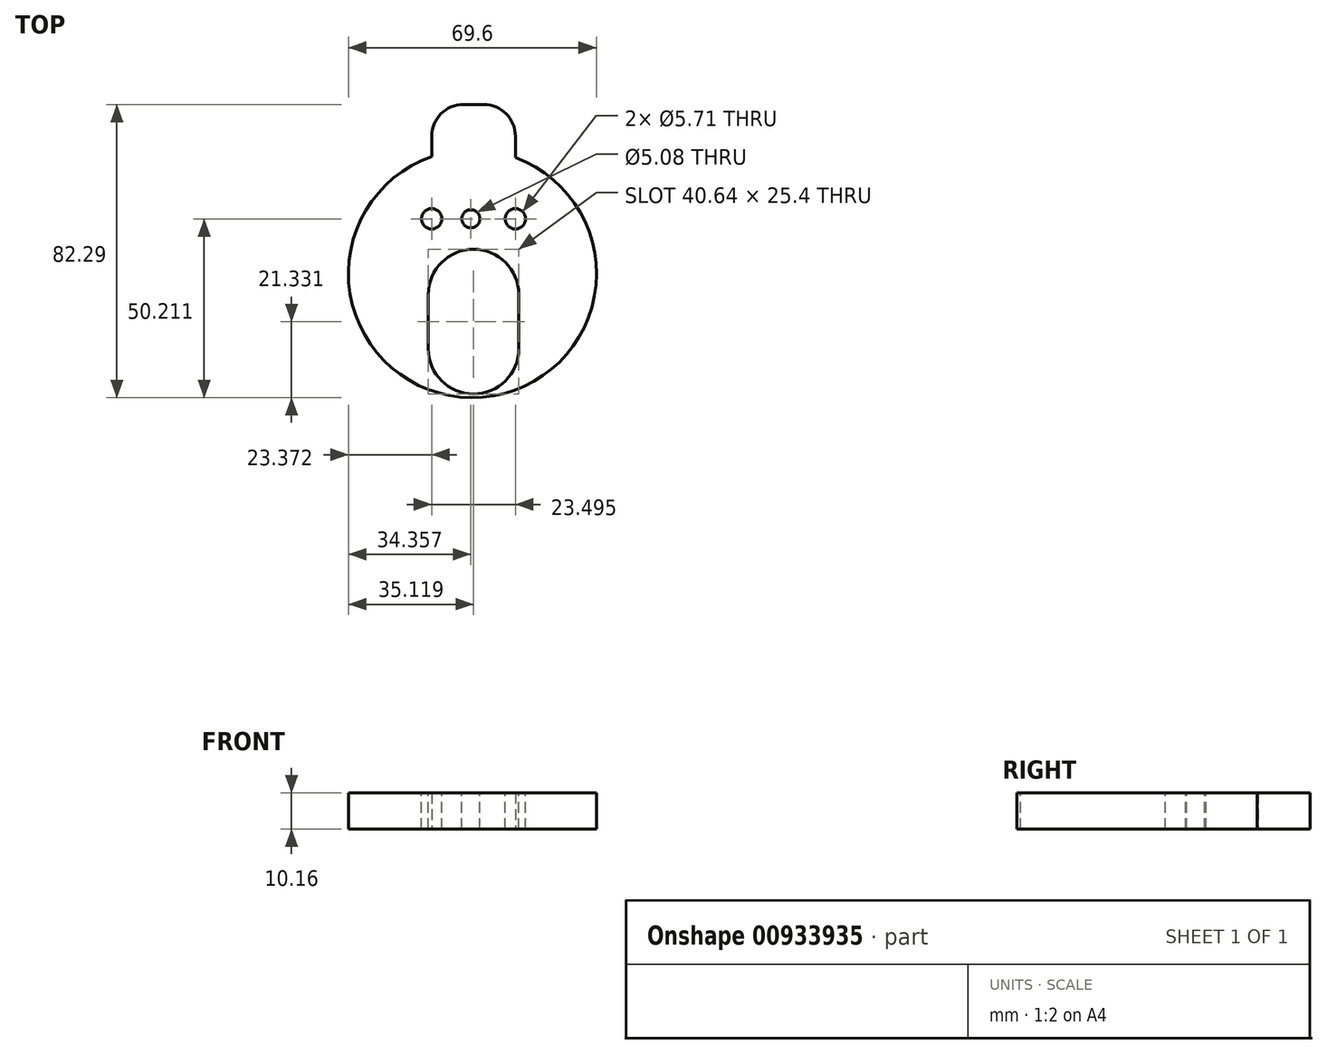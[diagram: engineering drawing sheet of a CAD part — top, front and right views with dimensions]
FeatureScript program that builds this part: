
annotation { "Feature Type Name" : "Feature", "Feature Type Description" : "" }
export const myFeature = defineFeature(function(context is Context, id is Id, definition is map)
    precondition{}
    {
        {
            var Q0;
            Q0=qCreatedBy(makeId("Top.planeOp"),FACE);
            var sketch = newSketch(context, id + "F0", { "sketchPlane" : qUnion([Q0])});
            skCircle(sketch, "E0", {"center": v(-10.4, -30.58) * mm, "radius": 34.8 * mm});
            skLineSegment(sketch, "E1", {"start": v(-21.84, 2.3) * mm, "end": v(-21.84, 16.92) * mm});
            skLineSegment(sketch, "E2", {"start": v(-21.84, 16.92) * mm, "end": v(1.66, 16.92) * mm});
            skLineSegment(sketch, "E3", {"start": v(1.66, 16.92) * mm, "end": v(1.66, 2.06) * mm});
            skSolve(sketch);
        }
        {
            var Q0;
            {var subQ0=sQuery(id+"F0.wireOp",EDGE,"E0");var subQ1=makeQuery(id+"F0.imprint","INTERSECT",VERTEX,{"derivedFrom":[subQ0,sQuery(id+"F0.wireOp",EDGE,"E1")]});Q0=makeQuery(id+"F0.imprint","IMPRINT",FACE,{"disambiguationData":[TD([[makeQuery(id+"F0.imprint","IMPRINT",EDGE,{"disambiguationData":[TD([[subQ1,1.0]])],"derivedFrom":subQ0}),1.0]])]});}
            var Q1;
            {var subQ0=sQuery(id+"F0.wireOp",EDGE,"E1");Q1=makeQuery(id+"F0.imprint","IMPRINT",FACE,{"disambiguationData":[TD([[makeQuery(id+"F0.imprint","IMPRINT",EDGE,{"derivedFrom":subQ0}),-1.0]])]});}
            extrude(context, id + "F1", {"entities" : qUnion([Q0, Q1]), "depth" : 10.16 * mm, "offsetDistance" : 25.4 * mm});
        }
        {
            var Q0;
            Q0=makeQuery(id+"F1.opExtrude","CAP_FACE",FACE,{"disambiguationData":[OSD([sQuery(id+"F0.wireOp",EDGE,"E0"),sQuery(id+"F0.wireOp",EDGE,"E1"),sQuery(id+"F0.wireOp",EDGE,"E2"),sQuery(id+"F0.wireOp",EDGE,"E3")])],"isStart":false});
            var sketch = newSketch(context, id + "F2", { "sketchPlane" : qUnion([Q0])});
            skCircle(sketch, "E4", {"center": v(1.66, -15.16) * mm, "radius": 2.86 * mm});
            skCircle(sketch, "E5", {"center": v(-21.84, -15.16) * mm, "radius": 2.86 * mm});
            skArc(sketch, "E6", {"start": v(2.6, -36.42) * mm, "mid": v(-10.1, -23.72) * mm, "end": v(-22.8, -36.42) * mm});
            skPoint(sketch, "E6.centerSnap0", {"position": v(-10.1, 16.92) * mm});
            skArc(sketch, "E7", {"start": v(-22.8, -51.66) * mm, "mid": v(-10.1, -64.36) * mm, "end": v(2.6, -51.66) * mm});
            skLineSegment(sketch, "E8", {"start": v(2.6, -36.42) * mm, "end": v(2.6, -51.66) * mm});
            skLineSegment(sketch, "E9", {"start": v(-22.8, -36.42) * mm, "end": v(-22.8, -51.66) * mm});
            skCircle(sketch, "E10", {"center": v(-10.85, -15.16) * mm, "radius": 2.54 * mm});
            skSolve(sketch);
        }
        {
            var Q0;
            Q0=makeQuery(id+"F2.imprint","IMPRINT",FACE,{"disambiguationData":[TD([[makeQuery(id+"F2.imprint","IMPRINT",EDGE,{"derivedFrom":sQuery(id+"F2.wireOp",EDGE,"E5")}),1.0]])]});
            var Q1;
            Q1=makeQuery(id+"F2.imprint","IMPRINT",FACE,{"disambiguationData":[TD([[makeQuery(id+"F2.imprint","IMPRINT",EDGE,{"derivedFrom":sQuery(id+"F2.wireOp",EDGE,"E10")}),1.0]])]});
            var Q2;
            Q2=makeQuery(id+"F2.imprint","IMPRINT",FACE,{"disambiguationData":[TD([[makeQuery(id+"F2.imprint","IMPRINT",EDGE,{"derivedFrom":sQuery(id+"F2.wireOp",EDGE,"E4")}),1.0]])]});
            var Q3;
            Q3=makeQuery(id+"F2.imprint","IMPRINT",FACE,{"disambiguationData":[TD([[makeQuery(id+"F2.imprint","IMPRINT",EDGE,{"derivedFrom":sQuery(id+"F2.wireOp",EDGE,"E6")}),1.0]])]});
            extrude(context, id + "F3", {"entities" : qUnion([Q0, Q1, Q2, Q3]), "operationType" : NewBodyOperationType.REMOVE, "oppositeDirection" : true, "depth" : 25.4 * mm, "offsetDistance" : 25.4 * mm});
        }
        {
            var Q0;
            Q0=makeQuery(id+"F1.opExtrude","SWEPT_EDGE",EDGE,{"disambiguationData":[OSD([sQuery(id+"F0.wireOp",EDGE,"E1"),sQuery(id+"F0.wireOp",EDGE,"E2")])]});
            var Q1;
            Q1=makeQuery(id+"F1.opExtrude","SWEPT_EDGE",EDGE,{"disambiguationData":[OSD([sQuery(id+"F0.wireOp",EDGE,"E2"),sQuery(id+"F0.wireOp",EDGE,"E3")])]});
            fillet(context, id + "F4", {"entities" : qUnion([Q0, Q1]), "radius" : 8.9 * mm, "tangentPropagation" : true, "allowEdgeOverflow" : false});
        }
    });
